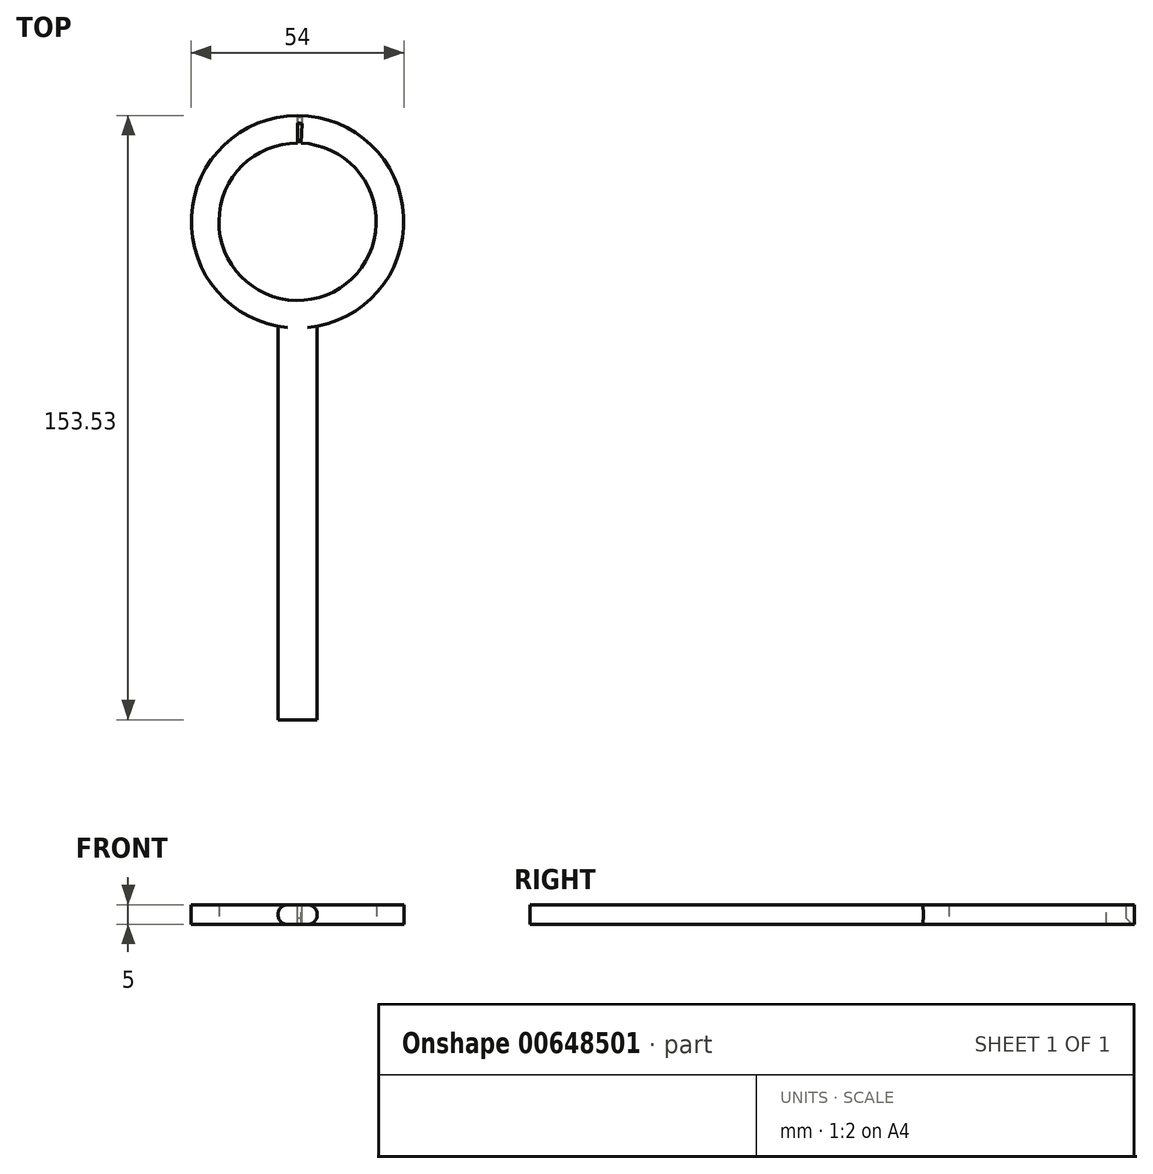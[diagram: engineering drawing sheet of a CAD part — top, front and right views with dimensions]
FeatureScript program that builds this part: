
annotation { "Feature Type Name" : "Feature", "Feature Type Description" : "" }
export const myFeature = defineFeature(function(context is Context, id is Id, definition is map)
    precondition{}
    {
        {
            var Q0;
            Q0=qCreatedBy(makeId("Top.planeOp"),FACE);
            var sketch = newSketch(context, id + "F0", { "sketchPlane" : qUnion([Q0])});
            skCircle(sketch, "E0", {"center": v(0, 0) * mm, "radius": 20 * mm});
            skCircle(sketch, "E1", {"center": v(0, 0) * mm, "radius": 27 * mm});
            skSolve(sketch);
        }
        {
            var Q0;
            Q0=makeQuery(id+"F0.imprint","IMPRINT",FACE,{"disambiguationData":[TD([[makeQuery(id+"F0.imprint","IMPRINT",EDGE,{"derivedFrom":sQuery(id+"F0.wireOp",EDGE,"E0")}),-1.0]])]});
            extrude(context, id + "F1", {"entities" : qUnion([Q0]), "depth" : 5 * mm, "offsetDistance" : 25 * mm});
        }
        {
            var Q0;
            Q0=makeQuery(id+"F1.opExtrude","CAP_FACE",FACE,{"disambiguationData":[OSD([sQuery(id+"F0.wireOp",EDGE,"E0"),sQuery(id+"F0.wireOp",EDGE,"E1")])],"isStart":false});
            var sketch = newSketch(context, id + "F2", { "sketchPlane" : qUnion([Q0])});
            skLineSegment(sketch, "E2", {"start": v(0, 20) * mm, "end": v(0, 25) * mm});
            skArc(sketch, "E3", {"start": v(1.1, 24.98) * mm, "mid": v(0.55, 25) * mm, "end": v(0, 25) * mm});
            skLineSegment(sketch, "E4", {"start": v(0.87, 19.98) * mm, "end": v(1.1, 24.98) * mm});
            skArc(sketch, "E5", {"start": v(0.87, 19.98) * mm, "mid": v(0.44, 20) * mm, "end": v(0, 20) * mm});
            skSolve(sketch);
        }
        {
            var Q0;
            Q0=qCreatedBy(makeId("Right.planeOp"),FACE);
            var sketch = newSketch(context, id + "F3", { "sketchPlane" : qUnion([Q0])});
            skLineSegment(sketch, "E6", {"start": v(0, 0) * mm, "end": v(0, 40) * mm, "construction": true});
            skSolve(sketch);
        }
        {
            var Q0;
            Q0=makeQuery(id+"F2.imprint","IMPRINT",FACE,{"disambiguationData":[TD([[makeQuery(id+"F2.imprint","IMPRINT",EDGE,{"derivedFrom":sQuery(id+"F2.wireOp",EDGE,"E2")}),-1.0]])]});
            extrude(context, id + "F4", {"entities" : qUnion([Q0]), "operationType" : NewBodyOperationType.REMOVE, "oppositeDirection" : true, "depth" : 6 * mm, "offsetDistance" : 25 * mm});
        }
        {
            var Q0;
            Q0=makeQuery(id+"F4.boolean.opBoolean","INTERSECT",EDGE,{"derivedFrom":[makeQuery(id+"F1.opExtrude","CAP_FACE",FACE,{"disambiguationData":[OSD([sQuery(id+"F0.wireOp",EDGE,"E0"),sQuery(id+"F0.wireOp",EDGE,"E1")])],"isStart":true}),makeQuery(id+"F4.opExtrude","SWEPT_FACE",FACE,{"disambiguationData":[OSD([sQuery(id+"F2.wireOp",EDGE,"E3")])]})]});
            var Q1;
            Q1=makeQuery(id+"F4.boolean.opBoolean","COPY",EDGE,{"derivedFrom":makeQuery(id+"F4.opExtrude","CAP_EDGE",EDGE,{"disambiguationData":[OSD([sQuery(id+"F2.wireOp",EDGE,"E3")])],"isStart":true})});
            chamfer(context, id + "F5", {"entities" : qUnion([Q0, Q1]), "width" : 1.5 * mm, "tangentPropagation" : true});
        }
        {
            var Q0;
            Q0=qCreatedBy(makeId("Top.planeOp"),FACE);
            var sketch = newSketch(context, id + "F6", { "sketchPlane" : qUnion([Q0])});
            skLineSegment(sketch, "E7.bottom", {"start": v(-5, -26.53) * mm, "end": v(5, -26.53) * mm});
            skLineSegment(sketch, "E7.top", {"start": v(-5, -126.53) * mm, "end": v(5, -126.53) * mm});
            skLineSegment(sketch, "E7.left", {"start": v(-5, -26.53) * mm, "end": v(-5, -126.53) * mm});
            skLineSegment(sketch, "E7.right", {"start": v(5, -26.53) * mm, "end": v(5, -126.53) * mm});
            skSolve(sketch);
        }
        {
            var Q0;
            Q0=makeQuery(id+"F6.imprint","IMPRINT",FACE,{"disambiguationData":[TD([[makeQuery(id+"F6.imprint","IMPRINT",EDGE,{"derivedFrom":sQuery(id+"F6.wireOp",EDGE,"E7.bottom")}),-1.0]])]});
            extrude(context, id + "F7", {"entities" : qUnion([Q0]), "operationType" : NewBodyOperationType.ADD, "depth" : 5 * mm, "offsetDistance" : 25 * mm});
        }
        {
            var Q0;
            Q0=makeQuery(id+"F7.opExtrude","CAP_EDGE",EDGE,{"disambiguationData":[OSD([sQuery(id+"F6.wireOp",EDGE,"E7.left")])],"isStart":false});
            var Q1;
            Q1=makeQuery(id+"F7.opExtrude","CAP_EDGE",EDGE,{"disambiguationData":[OSD([sQuery(id+"F6.wireOp",EDGE,"E7.right")])],"isStart":false});
            var Q2;
            Q2=makeQuery(id+"F7.opExtrude","CAP_EDGE",EDGE,{"disambiguationData":[OSD([sQuery(id+"F6.wireOp",EDGE,"E7.right")])],"isStart":true});
            var Q3;
            Q3=makeQuery(id+"F7.opExtrude","CAP_EDGE",EDGE,{"disambiguationData":[OSD([sQuery(id+"F6.wireOp",EDGE,"E7.left")])],"isStart":true});
            fillet(context, id + "F8", {"entities" : qUnion([Q0, Q1, Q2, Q3]), "radius" : 2.5 * mm, "tangentPropagation" : true, "allowEdgeOverflow" : false});
        }
    });
